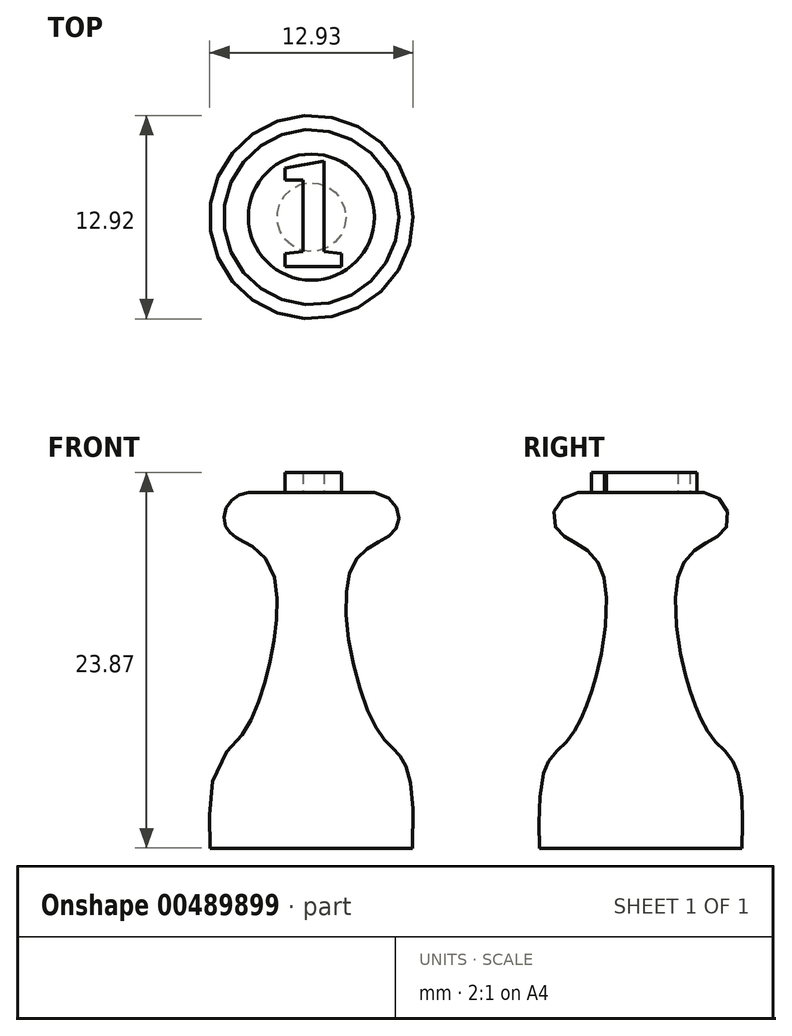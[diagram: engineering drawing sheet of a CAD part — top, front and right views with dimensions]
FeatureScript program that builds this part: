
annotation { "Feature Type Name" : "Feature", "Feature Type Description" : "" }
export const myFeature = defineFeature(function(context is Context, id is Id, definition is map)
    precondition{}
    {
        {
            var Q0;
            Q0=qCreatedBy(makeId("Front.planeOp"),FACE);
            var sketch = newSketch(context, id + "F0", { "sketchPlane" : qUnion([Q0])});
            skLineSegment(sketch, "E0", {"start": v(-40.46, 39.36) * mm, "end": v(-40.46, 16.79) * mm});
            skLineSegment(sketch, "E1", {"start": v(-40.46, 16.79) * mm, "end": v(-46.88, 16.79) * mm});
            skLineSegment(sketch, "E2", {"start": v(-40.46, 39.36) * mm, "end": v(-44.46, 39.36) * mm});
            skFitSpline(sketch, "E3", {"points": [v(-44.46, 39.36) * mm, v(-45.88, 37.16) * mm, v(-43.1, 34.8) * mm, v(-44.75, 24.12) * mm, v(-46.88, 16.79) * mm], "startDerivative": vector(-24.53, -3.05) * mm, "endDerivative": vector(2.67, -68.13) * mm});
            skLineSegment(sketch, "E4", {"start": v(-40.46, 44.25) * mm, "end": v(-40.46, 11.62) * mm, "construction": true});
            skSolve(sketch);
        }
        {
            var Q0;
            Q0=makeQuery(id+"F0.imprint","IMPRINT",FACE,{"disambiguationData":[TD([[makeQuery(id+"F0.imprint","IMPRINT",EDGE,{"derivedFrom":sQuery(id+"F0.wireOp",EDGE,"E0")}),-1.0]])]});
            var Q1;
            Q1=sQuery(id+"F0.wireOp",EDGE,"E4");
            revolve(context, id + "F1", {"entities" : qUnion([Q0]), "axis" : qUnion([Q1]), "revolveType" : RevolveType.FULL});
        }
        {
            var Q0;
            Q0=makeQuery(id+"F1.opRevolve","SWEPT_FACE",FACE,{"disambiguationData":[OSD([sQuery(id+"F0.wireOp",EDGE,"E2")])]});
            var sketch = newSketch(context, id + "F2", { "sketchPlane" : qUnion([Q0])});
            skText(sketch, "E5", { "text": "1", "fontName": "RobotoSlab-Bold.ttf"});
            const initialGuessF2  = {"E5": [-0.04243, -0.00313, 1, 0, 0.00678]};
            skSetInitialGuess(sketch, initialGuessF2);
            skSolve(sketch);
        }
        {
            var Q0;
            Q0=makeQuery(id+"F2.imprint","IMPRINT",FACE,{"disambiguationData":[TD([[makeQuery(id+"F2.imprint","IMPRINT",EDGE,{"derivedFrom":sQuery(id+"F2.wireOp",EDGE,"E5.sketch_text.stroke-0")}),-1.0]])]});
            extrude(context, id + "F3", {"entities" : qUnion([Q0]), "operationType" : NewBodyOperationType.ADD, "depth" : 1.3 * mm});
        }
    });
